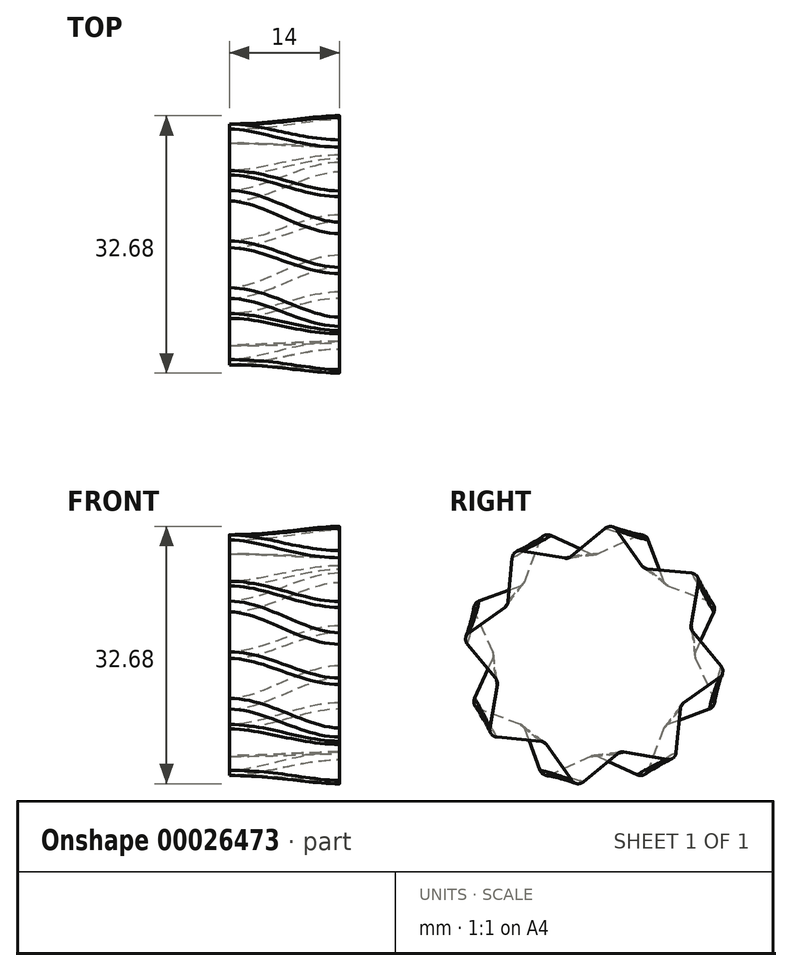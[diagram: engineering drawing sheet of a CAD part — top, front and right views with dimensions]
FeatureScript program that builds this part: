
annotation { "Feature Type Name" : "Feature", "Feature Type Description" : "" }
export const myFeature = defineFeature(function(context is Context, id is Id, definition is map)
    precondition{}
    {
        {
            var Q0;
            Q0=qCreatedBy(makeId("Right.planeOp"),FACE);
            var sketch = newSketch(context, id + "F0", { "sketchPlane" : qUnion([Q0])});
            skCircle(sketch, "E0", {"center": v(0, 0) * mm, "radius": 12.67 * mm});
            skLineSegment(sketch, "E1", {"start": v(0, 12.67) * mm, "end": v(6.48, 15.65) * mm});
            skLineSegment(sketch, "E2", {"start": v(6.48, 15.65) * mm, "end": v(8.96, 8.96) * mm});
            skLineSegment(sketch, "E3.1.0", {"start": v(-6.48, 15.65) * mm, "end": v(0, 12.67) * mm});
            skLineSegment(sketch, "E3.1.1", {"start": v(-8.96, 8.96) * mm, "end": v(-6.48, 15.65) * mm});
            skLineSegment(sketch, "E3.2.0", {"start": v(-15.65, 6.48) * mm, "end": v(-8.96, 8.96) * mm});
            skLineSegment(sketch, "E3.2.1", {"start": v(-12.67, 0) * mm, "end": v(-15.65, 6.48) * mm});
            skLineSegment(sketch, "E3.3.0", {"start": v(-15.65, -6.48) * mm, "end": v(-12.67, 0) * mm});
            skLineSegment(sketch, "E3.3.1", {"start": v(-8.96, -8.96) * mm, "end": v(-15.65, -6.48) * mm});
            skLineSegment(sketch, "E3.4.0", {"start": v(-6.48, -15.65) * mm, "end": v(-8.96, -8.96) * mm});
            skLineSegment(sketch, "E3.4.1", {"start": v(0, -12.67) * mm, "end": v(-6.48, -15.65) * mm});
            skLineSegment(sketch, "E3.5.0", {"start": v(6.48, -15.65) * mm, "end": v(0, -12.67) * mm});
            skLineSegment(sketch, "E3.5.1", {"start": v(8.96, -8.96) * mm, "end": v(6.48, -15.65) * mm});
            skLineSegment(sketch, "E3.6.0", {"start": v(15.65, -6.48) * mm, "end": v(8.96, -8.96) * mm});
            skLineSegment(sketch, "E3.6.1", {"start": v(12.67, 0) * mm, "end": v(15.65, -6.48) * mm});
            skLineSegment(sketch, "E3.7.0", {"start": v(15.65, 6.48) * mm, "end": v(12.67, 0) * mm});
            skLineSegment(sketch, "E3.7.1", {"start": v(8.96, 8.96) * mm, "end": v(15.65, 6.48) * mm});
            skSolve(sketch);
        }
        {
            var Q0;
            {var subQ1=sQuery(id+"F0.wireOp",EDGE,"E3.2.0");Q0=makeQuery(id+"F0.imprint","IMPRINT",FACE,{"disambiguationData":[TD([[makeQuery(id+"F0.imprint","IMPRINT",EDGE,{"derivedFrom":subQ1}),-1.0]])]});}
            var Q1;
            {var subQ1=sQuery(id+"F0.wireOp",EDGE,"E3.3.0");Q1=makeQuery(id+"F0.imprint","IMPRINT",FACE,{"disambiguationData":[TD([[makeQuery(id+"F0.imprint","IMPRINT",EDGE,{"derivedFrom":subQ1}),-1.0]])]});}
            var Q2;
            {var subQ1=sQuery(id+"F0.wireOp",EDGE,"E3.1.0");Q2=makeQuery(id+"F0.imprint","IMPRINT",FACE,{"disambiguationData":[TD([[makeQuery(id+"F0.imprint","IMPRINT",EDGE,{"derivedFrom":subQ1}),-1.0]])]});}
            var Q3;
            {var subQ1=sQuery(id+"F0.wireOp",EDGE,"E1");Q3=makeQuery(id+"F0.imprint","IMPRINT",FACE,{"disambiguationData":[TD([[makeQuery(id+"F0.imprint","IMPRINT",EDGE,{"derivedFrom":subQ1}),-1.0]])]});}
            var Q4;
            {var subQ1=sQuery(id+"F0.wireOp",EDGE,"E3.7.0");Q4=makeQuery(id+"F0.imprint","IMPRINT",FACE,{"disambiguationData":[TD([[makeQuery(id+"F0.imprint","IMPRINT",EDGE,{"derivedFrom":subQ1}),-1.0]])]});}
            var Q5;
            {var subQ1=sQuery(id+"F0.wireOp",EDGE,"E3.4.0");Q5=makeQuery(id+"F0.imprint","IMPRINT",FACE,{"disambiguationData":[TD([[makeQuery(id+"F0.imprint","IMPRINT",EDGE,{"derivedFrom":subQ1}),-1.0]])]});}
            var Q6;
            {var subQ1=sQuery(id+"F0.wireOp",EDGE,"E3.5.0");Q6=makeQuery(id+"F0.imprint","IMPRINT",FACE,{"disambiguationData":[TD([[makeQuery(id+"F0.imprint","IMPRINT",EDGE,{"derivedFrom":subQ1}),-1.0]])]});}
            var Q7;
            {var subQ1=sQuery(id+"F0.wireOp",EDGE,"E3.6.0");Q7=makeQuery(id+"F0.imprint","IMPRINT",FACE,{"disambiguationData":[TD([[makeQuery(id+"F0.imprint","IMPRINT",EDGE,{"derivedFrom":subQ1}),-1.0]])]});}
            var Q8;
            {var subQ0=sQuery(id+"F0.wireOp",EDGE,"E0");var subQ7=makeQuery(id+"F0.imprint","INTERSECT",VERTEX,{"derivedFrom":[subQ0,sQuery(id+"F0.wireOp",EDGE,"E2"),sQuery(id+"F0.wireOp",EDGE,"E3.7.1")]});Q8=makeQuery(id+"F0.imprint","IMPRINT",FACE,{"disambiguationData":[TD([[makeQuery(id+"F0.imprint","IMPRINT",EDGE,{"disambiguationData":[TD([[subQ7,1.0]])],"derivedFrom":subQ0}),1.0]])]});}
            var Q9;
            Q9=sQuery(id+"F0.wireOp",EDGE,"E3.5.1");
            var Q10;
            Q10=sQuery(id+"F0.wireOp",EDGE,"E3.7.1");
            var Q11;
            Q11=sQuery(id+"F0.wireOp",EDGE,"E3.2.1");
            var Q12;
            Q12=sQuery(id+"F0.wireOp",EDGE,"E3.2.0");
            var Q13;
            Q13=sQuery(id+"F0.wireOp",EDGE,"E3.3.0");
            var Q14;
            Q14=sQuery(id+"F0.wireOp",EDGE,"E3.3.1");
            var Q15;
            Q15=sQuery(id+"F0.wireOp",EDGE,"E3.4.0");
            var Q16;
            Q16=sQuery(id+"F0.wireOp",EDGE,"E3.4.1");
            var Q17;
            Q17=sQuery(id+"F0.wireOp",EDGE,"E3.5.0");
            var Q18;
            Q18=sQuery(id+"F0.wireOp",EDGE,"E1");
            var Q19;
            Q19=sQuery(id+"F0.wireOp",EDGE,"E3.1.1");
            var Q20;
            Q20=sQuery(id+"F0.wireOp",EDGE,"E0");
            var Q21;
            Q21=sQuery(id+"F0.wireOp",EDGE,"E3.1.0");
            var Q22;
            Q22=sQuery(id+"F0.wireOp",EDGE,"E3.7.0");
            var Q23;
            Q23=sQuery(id+"F0.wireOp",EDGE,"E3.6.1");
            var Q24;
            Q24=sQuery(id+"F0.wireOp",EDGE,"E2");
            var Q25;
            Q25=sQuery(id+"F0.wireOp",EDGE,"E3.6.0");
            extrude(context, id + "F1", {"entities" : qUnion([Q0, Q1, Q2, Q3, Q4, Q5, Q6, Q7, Q8]), "surfaceEntities" : qUnion([Q9, Q10, Q11, Q12, Q13, Q14, Q15, Q16, Q17, Q18, Q19, Q20, Q21, Q22, Q23, Q24, Q25]), "depth" : 1 * mm});
        }
        {
            var Q0;
            Q0=makeQuery(id+"F1.opExtrude","SWEPT_BODY",BODY,{"disambiguationData":[OSD([sQuery(id+"F0.wireOp",EDGE,"E1"),sQuery(id+"F0.wireOp",EDGE,"E2"),sQuery(id+"F0.wireOp",EDGE,"E3.1.0"),sQuery(id+"F0.wireOp",EDGE,"E3.1.1"),sQuery(id+"F0.wireOp",EDGE,"E3.2.0"),sQuery(id+"F0.wireOp",EDGE,"E3.2.1"),sQuery(id+"F0.wireOp",EDGE,"E3.3.0"),sQuery(id+"F0.wireOp",EDGE,"E3.3.1"),sQuery(id+"F0.wireOp",EDGE,"E3.4.0"),sQuery(id+"F0.wireOp",EDGE,"E3.4.1"),sQuery(id+"F0.wireOp",EDGE,"E3.5.0"),sQuery(id+"F0.wireOp",EDGE,"E3.5.1"),sQuery(id+"F0.wireOp",EDGE,"E3.6.0"),sQuery(id+"F0.wireOp",EDGE,"E3.6.1"),sQuery(id+"F0.wireOp",EDGE,"E3.7.0"),sQuery(id+"F0.wireOp",EDGE,"E3.7.1")])]});
            transform(context, id + "F2", {"entities" : qUnion([Q0]), "transformType" : TransformType.COPY});
        }
        {
            var Q0;
            Q0=qCreatedBy(makeId("Front.planeOp"),FACE);
            var sketch = newSketch(context, id + "F3", { "sketchPlane" : qUnion([Q0])});
            skLineSegment(sketch, "E4", {"start": v(0, 0) * mm, "end": v(-29.56, 0) * mm, "construction": true});
            skSolve(sketch);
        }
        {
            var Q0;
            Q0=makeQuery(id+"F2.opPattern","COPY",BODY,{"derivedFrom":makeQuery(id+"F1.opExtrude","SWEPT_BODY",BODY,{"disambiguationData":[OSD([sQuery(id+"F0.wireOp",EDGE,"E1"),sQuery(id+"F0.wireOp",EDGE,"E2"),sQuery(id+"F0.wireOp",EDGE,"E3.1.0"),sQuery(id+"F0.wireOp",EDGE,"E3.1.1"),sQuery(id+"F0.wireOp",EDGE,"E3.2.0"),sQuery(id+"F0.wireOp",EDGE,"E3.2.1"),sQuery(id+"F0.wireOp",EDGE,"E3.3.0"),sQuery(id+"F0.wireOp",EDGE,"E3.3.1"),sQuery(id+"F0.wireOp",EDGE,"E3.4.0"),sQuery(id+"F0.wireOp",EDGE,"E3.4.1"),sQuery(id+"F0.wireOp",EDGE,"E3.5.0"),sQuery(id+"F0.wireOp",EDGE,"E3.5.1"),sQuery(id+"F0.wireOp",EDGE,"E3.6.0"),sQuery(id+"F0.wireOp",EDGE,"E3.6.1"),sQuery(id+"F0.wireOp",EDGE,"E3.7.0"),sQuery(id+"F0.wireOp",EDGE,"E3.7.1")])]}),"instanceName":"1"});
            transform(context, id + "F4", {"entities" : qUnion([Q0]), "transformType" : TransformType.TRANSLATION_3D, "dx" : 15 * mm, "dy" : 0 * mm, "dz" : 0 * mm, "makeCopy" : false});
        }
        {
            var Q0;
            Q0=makeQuery(id+"F2.opPattern","COPY",BODY,{"derivedFrom":makeQuery(id+"F1.opExtrude","SWEPT_BODY",BODY,{"disambiguationData":[OSD([sQuery(id+"F0.wireOp",EDGE,"E1"),sQuery(id+"F0.wireOp",EDGE,"E2"),sQuery(id+"F0.wireOp",EDGE,"E3.1.0"),sQuery(id+"F0.wireOp",EDGE,"E3.1.1"),sQuery(id+"F0.wireOp",EDGE,"E3.2.0"),sQuery(id+"F0.wireOp",EDGE,"E3.2.1"),sQuery(id+"F0.wireOp",EDGE,"E3.3.0"),sQuery(id+"F0.wireOp",EDGE,"E3.3.1"),sQuery(id+"F0.wireOp",EDGE,"E3.4.0"),sQuery(id+"F0.wireOp",EDGE,"E3.4.1"),sQuery(id+"F0.wireOp",EDGE,"E3.5.0"),sQuery(id+"F0.wireOp",EDGE,"E3.5.1"),sQuery(id+"F0.wireOp",EDGE,"E3.6.0"),sQuery(id+"F0.wireOp",EDGE,"E3.6.1"),sQuery(id+"F0.wireOp",EDGE,"E3.7.0"),sQuery(id+"F0.wireOp",EDGE,"E3.7.1")])]}),"instanceName":"1"});
            var Q1;
            Q1=sQuery(id+"F3.wireOp",EDGE,"E4");
            transform(context, id + "F5", {"entities" : qUnion([Q0]), "transformType" : TransformType.ROTATION, "transformAxis" : qUnion([Q1]), "angle" : 120 * degree, "makeCopy" : false});
        }
        {
            var Q0;
            Q0=makeQuery(id+"F1.opExtrude","CAP_FACE",FACE,{"disambiguationData":[OSD([sQuery(id+"F0.wireOp",EDGE,"E1"),sQuery(id+"F0.wireOp",EDGE,"E2"),sQuery(id+"F0.wireOp",EDGE,"E3.1.0"),sQuery(id+"F0.wireOp",EDGE,"E3.1.1"),sQuery(id+"F0.wireOp",EDGE,"E3.2.0"),sQuery(id+"F0.wireOp",EDGE,"E3.2.1"),sQuery(id+"F0.wireOp",EDGE,"E3.3.0"),sQuery(id+"F0.wireOp",EDGE,"E3.3.1"),sQuery(id+"F0.wireOp",EDGE,"E3.4.0"),sQuery(id+"F0.wireOp",EDGE,"E3.4.1"),sQuery(id+"F0.wireOp",EDGE,"E3.5.0"),sQuery(id+"F0.wireOp",EDGE,"E3.5.1"),sQuery(id+"F0.wireOp",EDGE,"E3.6.0"),sQuery(id+"F0.wireOp",EDGE,"E3.6.1"),sQuery(id+"F0.wireOp",EDGE,"E3.7.0"),sQuery(id+"F0.wireOp",EDGE,"E3.7.1")])],"isStart":false});
            var Q1;
            Q1=makeQuery(id+"F2.opPattern","COPY",FACE,{"derivedFrom":makeQuery(id+"F1.opExtrude","CAP_FACE",FACE,{"disambiguationData":[OSD([sQuery(id+"F0.wireOp",EDGE,"E1"),sQuery(id+"F0.wireOp",EDGE,"E2"),sQuery(id+"F0.wireOp",EDGE,"E3.1.0"),sQuery(id+"F0.wireOp",EDGE,"E3.1.1"),sQuery(id+"F0.wireOp",EDGE,"E3.2.0"),sQuery(id+"F0.wireOp",EDGE,"E3.2.1"),sQuery(id+"F0.wireOp",EDGE,"E3.3.0"),sQuery(id+"F0.wireOp",EDGE,"E3.3.1"),sQuery(id+"F0.wireOp",EDGE,"E3.4.0"),sQuery(id+"F0.wireOp",EDGE,"E3.4.1"),sQuery(id+"F0.wireOp",EDGE,"E3.5.0"),sQuery(id+"F0.wireOp",EDGE,"E3.5.1"),sQuery(id+"F0.wireOp",EDGE,"E3.6.0"),sQuery(id+"F0.wireOp",EDGE,"E3.6.1"),sQuery(id+"F0.wireOp",EDGE,"E3.7.0"),sQuery(id+"F0.wireOp",EDGE,"E3.7.1")])],"isStart":true}),"instanceName":"1"});
            loft(context, id + "F6", {"startCondition" : LoftEndDerivativeType.NORMAL_TO_PROFILE, "startMagnitude" : 1, "endCondition" : LoftEndDerivativeType.NORMAL_TO_PROFILE, "endMagnitude" : 1, "sheetProfilesArray" : [{ "sheetProfileEntities" : qUnion([Q0]) }, { "sheetProfileEntities" : qUnion([Q1]) }]});
        }
        {
            var Q0;
            Q0=makeQuery(id+"F1.opExtrude","SWEPT_BODY",BODY,{"disambiguationData":[OSD([sQuery(id+"F0.wireOp",EDGE,"E1"),sQuery(id+"F0.wireOp",EDGE,"E2"),sQuery(id+"F0.wireOp",EDGE,"E3.1.0"),sQuery(id+"F0.wireOp",EDGE,"E3.1.1"),sQuery(id+"F0.wireOp",EDGE,"E3.2.0"),sQuery(id+"F0.wireOp",EDGE,"E3.2.1"),sQuery(id+"F0.wireOp",EDGE,"E3.3.0"),sQuery(id+"F0.wireOp",EDGE,"E3.3.1"),sQuery(id+"F0.wireOp",EDGE,"E3.4.0"),sQuery(id+"F0.wireOp",EDGE,"E3.4.1"),sQuery(id+"F0.wireOp",EDGE,"E3.5.0"),sQuery(id+"F0.wireOp",EDGE,"E3.5.1"),sQuery(id+"F0.wireOp",EDGE,"E3.6.0"),sQuery(id+"F0.wireOp",EDGE,"E3.6.1"),sQuery(id+"F0.wireOp",EDGE,"E3.7.0"),sQuery(id+"F0.wireOp",EDGE,"E3.7.1")])]});
            deleteBodies(context, id + "F7", {"entities" : qUnion([Q0])});
        }
        {
            var Q0;
            Q0=makeQuery(id+"F2.opPattern","COPY",BODY,{"derivedFrom":makeQuery(id+"F1.opExtrude","SWEPT_BODY",BODY,{"disambiguationData":[OSD([sQuery(id+"F0.wireOp",EDGE,"E1"),sQuery(id+"F0.wireOp",EDGE,"E2"),sQuery(id+"F0.wireOp",EDGE,"E3.1.0"),sQuery(id+"F0.wireOp",EDGE,"E3.1.1"),sQuery(id+"F0.wireOp",EDGE,"E3.2.0"),sQuery(id+"F0.wireOp",EDGE,"E3.2.1"),sQuery(id+"F0.wireOp",EDGE,"E3.3.0"),sQuery(id+"F0.wireOp",EDGE,"E3.3.1"),sQuery(id+"F0.wireOp",EDGE,"E3.4.0"),sQuery(id+"F0.wireOp",EDGE,"E3.4.1"),sQuery(id+"F0.wireOp",EDGE,"E3.5.0"),sQuery(id+"F0.wireOp",EDGE,"E3.5.1"),sQuery(id+"F0.wireOp",EDGE,"E3.6.0"),sQuery(id+"F0.wireOp",EDGE,"E3.6.1"),sQuery(id+"F0.wireOp",EDGE,"E3.7.0"),sQuery(id+"F0.wireOp",EDGE,"E3.7.1")])]}),"instanceName":"1"});
            deleteBodies(context, id + "F8", {"entities" : qUnion([Q0])});
        }
        {
            var Q0;
            Q0=makeQuery(id+"F6.opLoft","SWEPT_EDGE",EDGE,{"disambiguationData":[OSD([sQuery(id+"F0.wireOp",EDGE,"E3.4.0"),sQuery(id+"F0.wireOp",EDGE,"E3.4.1"),sQuery(id+"F0.wireOp",EDGE,"E3.5.0"),sQuery(id+"F0.wireOp",EDGE,"E3.5.1")])]});
            var Q1;
            Q1=makeQuery(id+"F6.opLoft","SWEPT_EDGE",EDGE,{"disambiguationData":[OSD([sQuery(id+"F0.wireOp",EDGE,"E3.3.0"),sQuery(id+"F0.wireOp",EDGE,"E3.3.1"),sQuery(id+"F0.wireOp",EDGE,"E3.4.0"),sQuery(id+"F0.wireOp",EDGE,"E3.4.1")])]});
            var Q2;
            Q2=makeQuery(id+"F6.opLoft","SWEPT_EDGE",EDGE,{"disambiguationData":[OSD([sQuery(id+"F0.wireOp",EDGE,"E3.5.0"),sQuery(id+"F0.wireOp",EDGE,"E3.5.1"),sQuery(id+"F0.wireOp",EDGE,"E3.6.0"),sQuery(id+"F0.wireOp",EDGE,"E3.6.1")])]});
            var Q3;
            Q3=makeQuery(id+"F6.opLoft","SWEPT_EDGE",EDGE,{"disambiguationData":[OSD([sQuery(id+"F0.wireOp",EDGE,"E3.2.0"),sQuery(id+"F0.wireOp",EDGE,"E3.2.1"),sQuery(id+"F0.wireOp",EDGE,"E3.3.0"),sQuery(id+"F0.wireOp",EDGE,"E3.3.1")])]});
            var Q4;
            Q4=makeQuery(id+"F6.opLoft","SWEPT_EDGE",EDGE,{"disambiguationData":[OSD([sQuery(id+"F0.wireOp",EDGE,"E3.1.0"),sQuery(id+"F0.wireOp",EDGE,"E3.1.1"),sQuery(id+"F0.wireOp",EDGE,"E3.2.0"),sQuery(id+"F0.wireOp",EDGE,"E3.2.1")])]});
            var Q5;
            Q5=makeQuery(id+"F6.opLoft","SWEPT_EDGE",EDGE,{"disambiguationData":[OSD([sQuery(id+"F0.wireOp",EDGE,"E1"),sQuery(id+"F0.wireOp",EDGE,"E2"),sQuery(id+"F0.wireOp",EDGE,"E3.1.0"),sQuery(id+"F0.wireOp",EDGE,"E3.1.1")])]});
            var Q6;
            Q6=makeQuery(id+"F6.opLoft","SWEPT_EDGE",EDGE,{"disambiguationData":[OSD([sQuery(id+"F0.wireOp",EDGE,"E1"),sQuery(id+"F0.wireOp",EDGE,"E2"),sQuery(id+"F0.wireOp",EDGE,"E3.7.0"),sQuery(id+"F0.wireOp",EDGE,"E3.7.1")])]});
            var Q7;
            Q7=makeQuery(id+"F6.opLoft","SWEPT_EDGE",EDGE,{"disambiguationData":[OSD([sQuery(id+"F0.wireOp",EDGE,"E3.6.0"),sQuery(id+"F0.wireOp",EDGE,"E3.6.1"),sQuery(id+"F0.wireOp",EDGE,"E3.7.0"),sQuery(id+"F0.wireOp",EDGE,"E3.7.1")])]});
            fillet(context, id + "F9", {"entities" : qUnion([Q0, Q1, Q2, Q3, Q4, Q5, Q6, Q7]), "radius" : 1 * mm, "tangentPropagation" : true, "allowEdgeOverflow" : false});
        }
        {
            var Q0;
            Q0=makeQuery(id+"F6.opLoft","SWEPT_EDGE",EDGE,{"disambiguationData":[OSD([sQuery(id+"F0.wireOp",EDGE,"E0"),sQuery(id+"F0.wireOp",EDGE,"E1"),sQuery(id+"F0.wireOp",EDGE,"E3.1.0"),sQuery(id+"F0.wireOp",EDGE,"E3.1.1"),sQuery(id+"F0.wireOp",EDGE,"E3.2.0")])]});
            var Q1;
            Q1=makeQuery(id+"F6.opLoft","SWEPT_EDGE",EDGE,{"disambiguationData":[OSD([sQuery(id+"F0.wireOp",EDGE,"E0"),sQuery(id+"F0.wireOp",EDGE,"E3.1.1"),sQuery(id+"F0.wireOp",EDGE,"E3.2.0"),sQuery(id+"F0.wireOp",EDGE,"E3.2.1"),sQuery(id+"F0.wireOp",EDGE,"E3.3.0")])]});
            var Q2;
            Q2=makeQuery(id+"F6.opLoft","SWEPT_EDGE",EDGE,{"disambiguationData":[OSD([sQuery(id+"F0.wireOp",EDGE,"E0"),sQuery(id+"F0.wireOp",EDGE,"E3.2.1"),sQuery(id+"F0.wireOp",EDGE,"E3.3.0"),sQuery(id+"F0.wireOp",EDGE,"E3.3.1"),sQuery(id+"F0.wireOp",EDGE,"E3.4.0")])]});
            var Q3;
            Q3=makeQuery(id+"F6.opLoft","SWEPT_EDGE",EDGE,{"disambiguationData":[OSD([sQuery(id+"F0.wireOp",EDGE,"E0"),sQuery(id+"F0.wireOp",EDGE,"E3.3.1"),sQuery(id+"F0.wireOp",EDGE,"E3.4.0"),sQuery(id+"F0.wireOp",EDGE,"E3.4.1"),sQuery(id+"F0.wireOp",EDGE,"E3.5.0")])]});
            var Q4;
            Q4=makeQuery(id+"F6.opLoft","SWEPT_EDGE",EDGE,{"disambiguationData":[OSD([sQuery(id+"F0.wireOp",EDGE,"E0"),sQuery(id+"F0.wireOp",EDGE,"E3.4.1"),sQuery(id+"F0.wireOp",EDGE,"E3.5.0"),sQuery(id+"F0.wireOp",EDGE,"E3.5.1"),sQuery(id+"F0.wireOp",EDGE,"E3.6.0")])]});
            var Q5;
            Q5=makeQuery(id+"F6.opLoft","SWEPT_EDGE",EDGE,{"disambiguationData":[OSD([sQuery(id+"F0.wireOp",EDGE,"E0"),sQuery(id+"F0.wireOp",EDGE,"E3.5.1"),sQuery(id+"F0.wireOp",EDGE,"E3.6.0"),sQuery(id+"F0.wireOp",EDGE,"E3.6.1"),sQuery(id+"F0.wireOp",EDGE,"E3.7.0")])]});
            var Q6;
            Q6=makeQuery(id+"F6.opLoft","SWEPT_EDGE",EDGE,{"disambiguationData":[OSD([sQuery(id+"F0.wireOp",EDGE,"E0"),sQuery(id+"F0.wireOp",EDGE,"E2"),sQuery(id+"F0.wireOp",EDGE,"E3.6.1"),sQuery(id+"F0.wireOp",EDGE,"E3.7.0"),sQuery(id+"F0.wireOp",EDGE,"E3.7.1")])]});
            var Q7;
            Q7=makeQuery(id+"F6.opLoft","SWEPT_EDGE",EDGE,{"disambiguationData":[OSD([sQuery(id+"F0.wireOp",EDGE,"E0"),sQuery(id+"F0.wireOp",EDGE,"E1"),sQuery(id+"F0.wireOp",EDGE,"E2"),sQuery(id+"F0.wireOp",EDGE,"E3.1.0"),sQuery(id+"F0.wireOp",EDGE,"E3.7.1")])]});
            fillet(context, id + "F10", {"entities" : qUnion([Q0, Q1, Q2, Q3, Q4, Q5, Q6, Q7]), "radius" : 1 * mm, "tangentPropagation" : true, "allowEdgeOverflow" : false});
        }
    });
